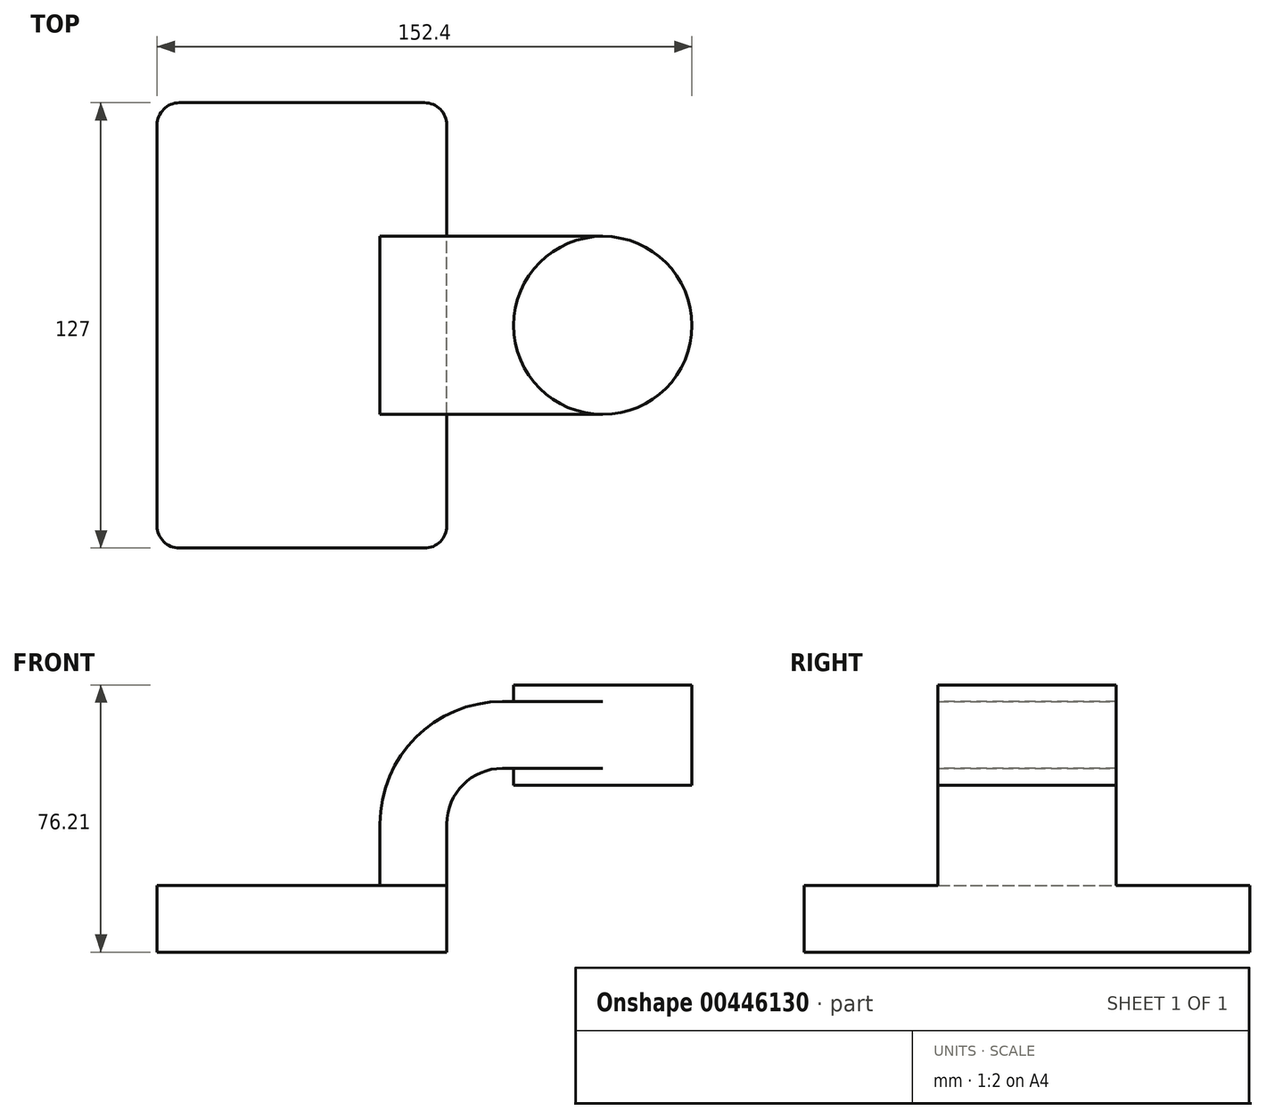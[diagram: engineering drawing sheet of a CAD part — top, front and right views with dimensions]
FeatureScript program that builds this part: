
annotation { "Feature Type Name" : "Feature", "Feature Type Description" : "" }
export const myFeature = defineFeature(function(context is Context, id is Id, definition is map)
    precondition{}
    {
        {
            var Q0;
            Q0=qCreatedBy(makeId("Front.planeOp"),FACE);
            var sketch = newSketch(context, id + "F0", { "sketchPlane" : qUnion([Q0])});
            skLineSegment(sketch, "E0.bottom", {"start": v(41.28, -9.52) * mm, "end": v(-41.28, -9.53) * mm});
            skLineSegment(sketch, "E0.top", {"start": v(41.28, 9.53) * mm, "end": v(-41.28, 9.52) * mm});
            skLineSegment(sketch, "E0.left", {"start": v(41.28, -9.52) * mm, "end": v(41.28, 9.53) * mm});
            skLineSegment(sketch, "E0.right", {"start": v(-41.28, -9.53) * mm, "end": v(-41.28, 9.52) * mm});
            skPoint(sketch, "E0.middle", {"position": v(0, 0) * mm});
            skLineSegment(sketch, "E1", {"start": v(41.28, 9.53) * mm, "end": v(41.28, 27) * mm});
            skLineSegment(sketch, "E2.bottom", {"start": v(111.12, 38.1) * mm, "end": v(60.32, 38.1) * mm});
            skLineSegment(sketch, "E2.top", {"start": v(111.12, 66.68) * mm, "end": v(60.32, 66.68) * mm});
            skLineSegment(sketch, "E2.left", {"start": v(111.12, 38.1) * mm, "end": v(111.12, 66.68) * mm});
            skLineSegment(sketch, "E2.right", {"start": v(60.32, 38.1) * mm, "end": v(60.32, 66.68) * mm});
            skPoint(sketch, "E2.middle", {"position": v(85.72, 52.39) * mm});
            skArc(sketch, "E3", {"start": v(41.28, 27) * mm, "mid": v(45.92, 38.23) * mm, "end": v(57.15, 42.88) * mm});
            skLineSegment(sketch, "E4.0", {"start": v(57.15, 61.93) * mm, "end": v(85.73, 61.93) * mm});
            skArc(sketch, "E4.1", {"start": v(22.23, 27) * mm, "mid": v(32.45, 51.7) * mm, "end": v(57.15, 61.93) * mm});
            skLineSegment(sketch, "E4.2", {"start": v(22.23, 9.53) * mm, "end": v(22.23, 27) * mm});
            skLineSegment(sketch, "E5", {"start": v(57.15, 42.88) * mm, "end": v(85.73, 42.88) * mm});
            skLineSegment(sketch, "E6", {"start": v(85.72, 66.68) * mm, "end": v(85.72, 38.1) * mm});
            skFitSpline(sketch, "E7", {"points": [v(-41.28, 9.52) * mm, v(57.15, 61.93) * mm], "startDerivative": vector(56.95, 104.7) * mm, "endDerivative": vector(136.19, -18.44) * mm});
            skSolve(sketch);
        }
        {
            var Q0;
            Q0=makeQuery(id+"F0.imprint","IMPRINT",FACE,{"disambiguationData":[TD([[makeQuery(id+"F0.imprint","IMPRINT",EDGE,{"derivedFrom":sQuery(id+"F0.wireOp",EDGE,"E0.bottom")}),-1.0]])]});
            extrude(context, id + "F1", {"entities" : qUnion([Q0]), "endBound" : BoundingType.SYMMETRIC, "depth" : 127 * mm});
        }
        {
            var Q0;
            {var subQ6=sQuery(id+"F0.wireOp",EDGE,"E1");Q0=makeQuery(id+"F0.imprint","IMPRINT",FACE,{"disambiguationData":[TD([[makeQuery(id+"F0.imprint","IMPRINT",EDGE,{"derivedFrom":subQ6}),1.0]])]});}
            var Q1;
            {var subQ0=sQuery(id+"F0.wireOp",EDGE,"E5");var subQ1=sQuery(id+"F0.wireOp",EDGE,"E2.right");var subQ2=makeQuery(id+"F0.imprint","INTERSECT",VERTEX,{"derivedFrom":[subQ1,subQ0]});Q1=makeQuery(id+"F0.imprint","IMPRINT",FACE,{"disambiguationData":[TD([[makeQuery(id+"F0.imprint","IMPRINT",EDGE,{"disambiguationData":[TD([[subQ2,-1.0]])],"derivedFrom":subQ1}),-1.0]])]});}
            extrude(context, id + "F2", {"entities" : qUnion([Q0, Q1]), "operationType" : NewBodyOperationType.ADD, "endBound" : BoundingType.SYMMETRIC, "depth" : 50.8 * mm});
        }
        {
            var Q0;
            Q0=makeQuery(id+"F0.imprint","IMPRINT",FACE,{"disambiguationData":[TD([[makeQuery(id+"F0.imprint","IMPRINT",EDGE,{"derivedFrom":sQuery(id+"F0.wireOp",EDGE,"E4.1")}),1.0]])]});
            extrude(context, id + "F3", {"entities" : qUnion([Q0]), "operationType" : NewBodyOperationType.ADD, "endBound" : BoundingType.SYMMETRIC, "depth" : 15.88 * mm});
        }
        {
            var Q0;
            {var subQ0=sQuery(id+"F0.wireOp",EDGE,"E2.left");Q0=makeQuery(id+"F0.imprint","IMPRINT",FACE,{"disambiguationData":[TD([[makeQuery(id+"F0.imprint","IMPRINT",EDGE,{"derivedFrom":subQ0}),1.0]])]});}
            var Q1;
            Q1=sQuery(id+"F0.wireOp",EDGE,"E6");
            revolve(context, id + "F4", {"operationType" : NewBodyOperationType.ADD, "entities" : qUnion([Q0]), "axis" : qUnion([Q1]), "revolveType" : RevolveType.FULL});
        }
        {
            var Q0;
            Q0=makeQuery(id+"F1.opExtrude","CAP_EDGE",EDGE,{"disambiguationData":[OSD([sQuery(id+"F0.wireOp",EDGE,"E0.right")])],"isStart":false});
            var Q1;
            Q1=makeQuery(id+"F1.opExtrude","CAP_EDGE",EDGE,{"disambiguationData":[OSD([sQuery(id+"F0.wireOp",EDGE,"E0.left")])],"isStart":false});
            var Q2;
            Q2=makeQuery(id+"F1.opExtrude","CAP_EDGE",EDGE,{"disambiguationData":[OSD([sQuery(id+"F0.wireOp",EDGE,"E0.right")])],"isStart":true});
            var Q3;
            Q3=makeQuery(id+"F1.opExtrude","CAP_EDGE",EDGE,{"disambiguationData":[OSD([sQuery(id+"F0.wireOp",EDGE,"E0.left")])],"isStart":true});
            fillet(context, id + "F5", {"entities" : qUnion([Q0, Q1, Q2, Q3]), "radius" : 6.35 * mm, "tangentPropagation" : true, "allowEdgeOverflow" : false});
        }
    });
